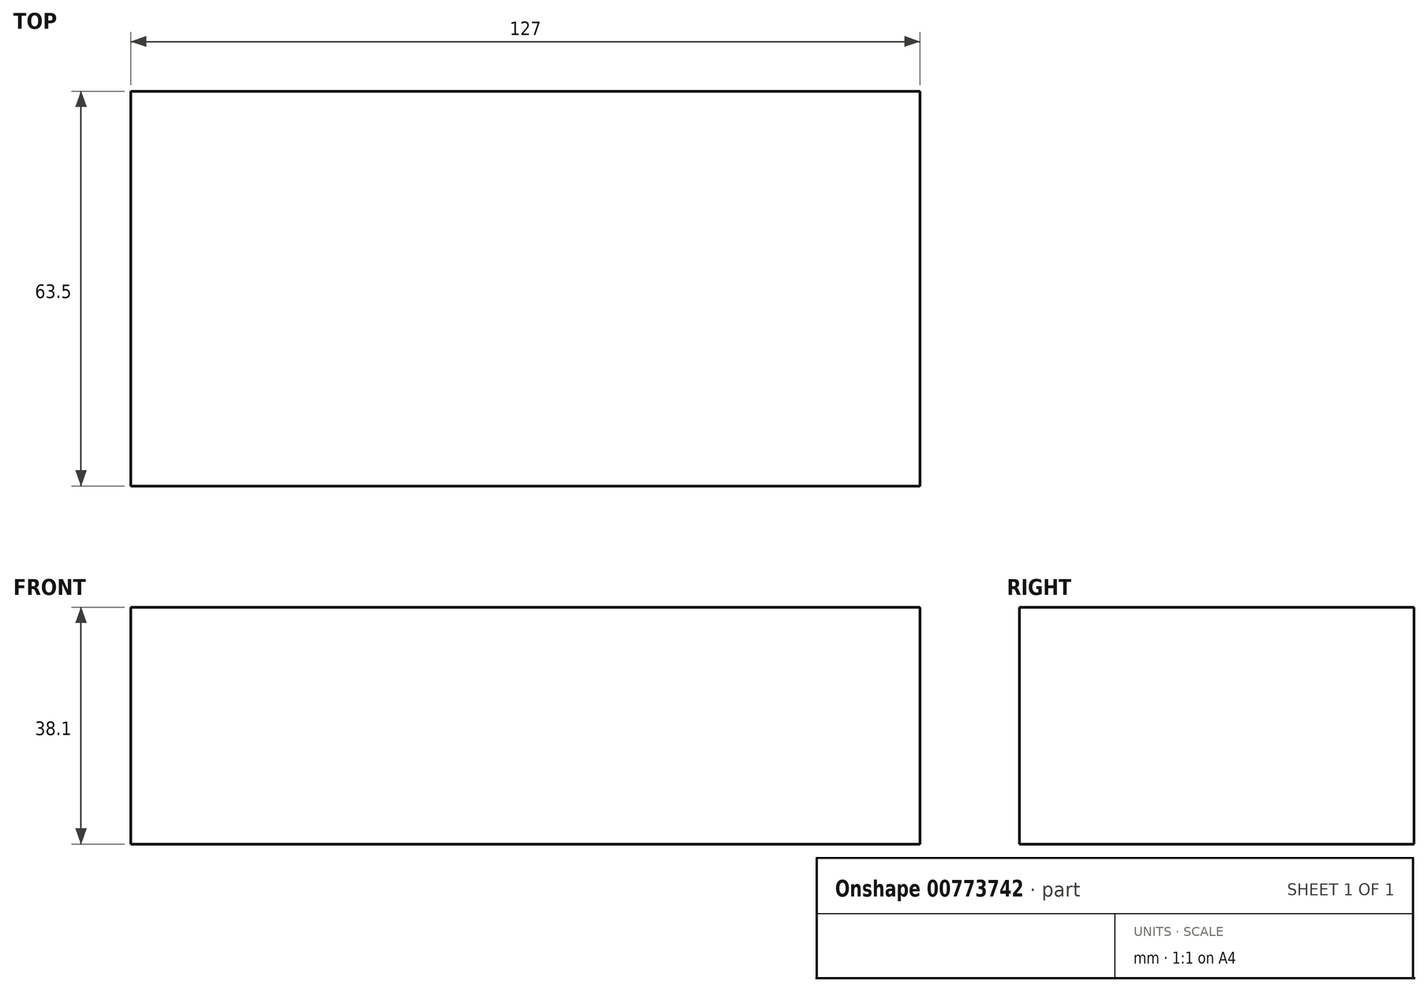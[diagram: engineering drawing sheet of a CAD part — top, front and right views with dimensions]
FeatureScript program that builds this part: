
annotation { "Feature Type Name" : "Feature", "Feature Type Description" : "" }
export const myFeature = defineFeature(function(context is Context, id is Id, definition is map)
    precondition{}
    {
        {
            var Q0;
            Q0=qCreatedBy(makeId("Front.planeOp"),FACE);
            var sketch = newSketch(context, id + "F0", { "sketchPlane" : qUnion([Q0])});
            skLineSegment(sketch, "E0.bottom", {"start": v(-60.5, 15.71) * mm, "end": v(66.5, 15.71) * mm});
            skLineSegment(sketch, "E0.top", {"start": v(-60.5, -22.39) * mm, "end": v(66.5, -22.39) * mm});
            skLineSegment(sketch, "E0.left", {"start": v(-60.5, 15.71) * mm, "end": v(-60.5, -22.39) * mm});
            skLineSegment(sketch, "E0.right", {"start": v(66.5, 15.71) * mm, "end": v(66.5, -22.39) * mm});
            skSolve(sketch);
        }
        {
            var Q0;
            Q0 = qSketchRegion(id + "F0", true);
            extrude(context, id + "F1", {"entities" : qUnion([Q0]), "depth" : 63.5 * mm, "offsetDistance" : 25.4 * mm});
        }
    });
